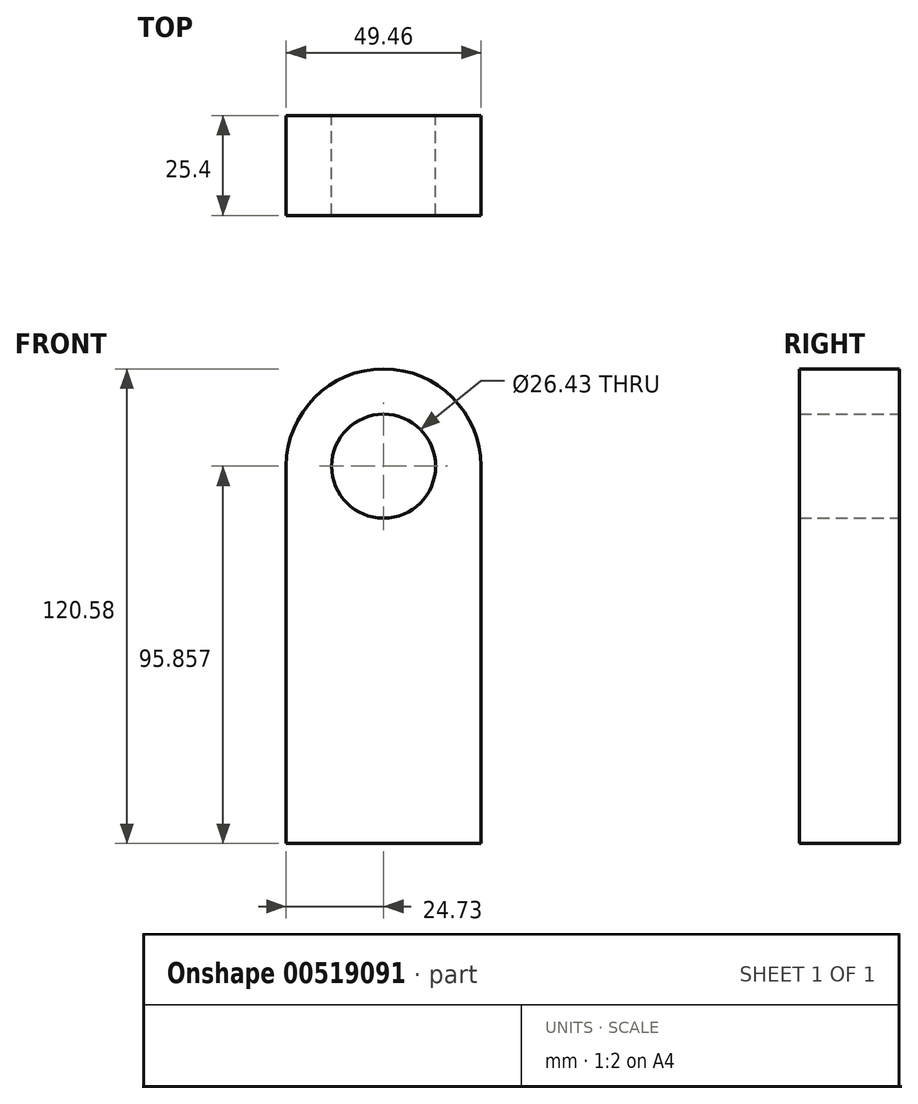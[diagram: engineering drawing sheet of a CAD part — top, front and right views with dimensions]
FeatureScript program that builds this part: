
annotation { "Feature Type Name" : "Feature", "Feature Type Description" : "" }
export const myFeature = defineFeature(function(context is Context, id is Id, definition is map)
    precondition{}
    {
        {
            var Q0;
            Q0=qCreatedBy(makeId("Front.planeOp"),FACE);
            var sketch = newSketch(context, id + "F0", { "sketchPlane" : qUnion([Q0])});
            skLineSegment(sketch, "E0.top", {"start": v(24.73, -47.93) * mm, "end": v(-24.73, -47.93) * mm});
            skLineSegment(sketch, "E0.left", {"start": v(24.73, 47.93) * mm, "end": v(24.73, -47.93) * mm});
            skLineSegment(sketch, "E0.right", {"start": v(-24.73, 47.93) * mm, "end": v(-24.73, -47.93) * mm});
            skPoint(sketch, "E0.middle", {"position": v(0, 0) * mm});
            skArc(sketch, "E1", {"start": v(24.73, 47.93) * mm, "mid": v(0, 72.65) * mm, "end": v(-24.73, 47.93) * mm});
            skCircle(sketch, "E2", {"center": v(0, 47.93) * mm, "radius": 13.21 * mm});
            skSolve(sketch);
        }
        {
            var Q0;
            Q0=makeQuery(id+"F0.imprint","IMPRINT",FACE,{"disambiguationData":[TD([[makeQuery(id+"F0.imprint","IMPRINT",EDGE,{"derivedFrom":sQuery(id+"F0.wireOp",EDGE,"E0.top")}),-1.0]])]});
            extrude(context, id + "F1", {"entities" : qUnion([Q0]), "depth" : 25.4 * mm});
        }
    });
